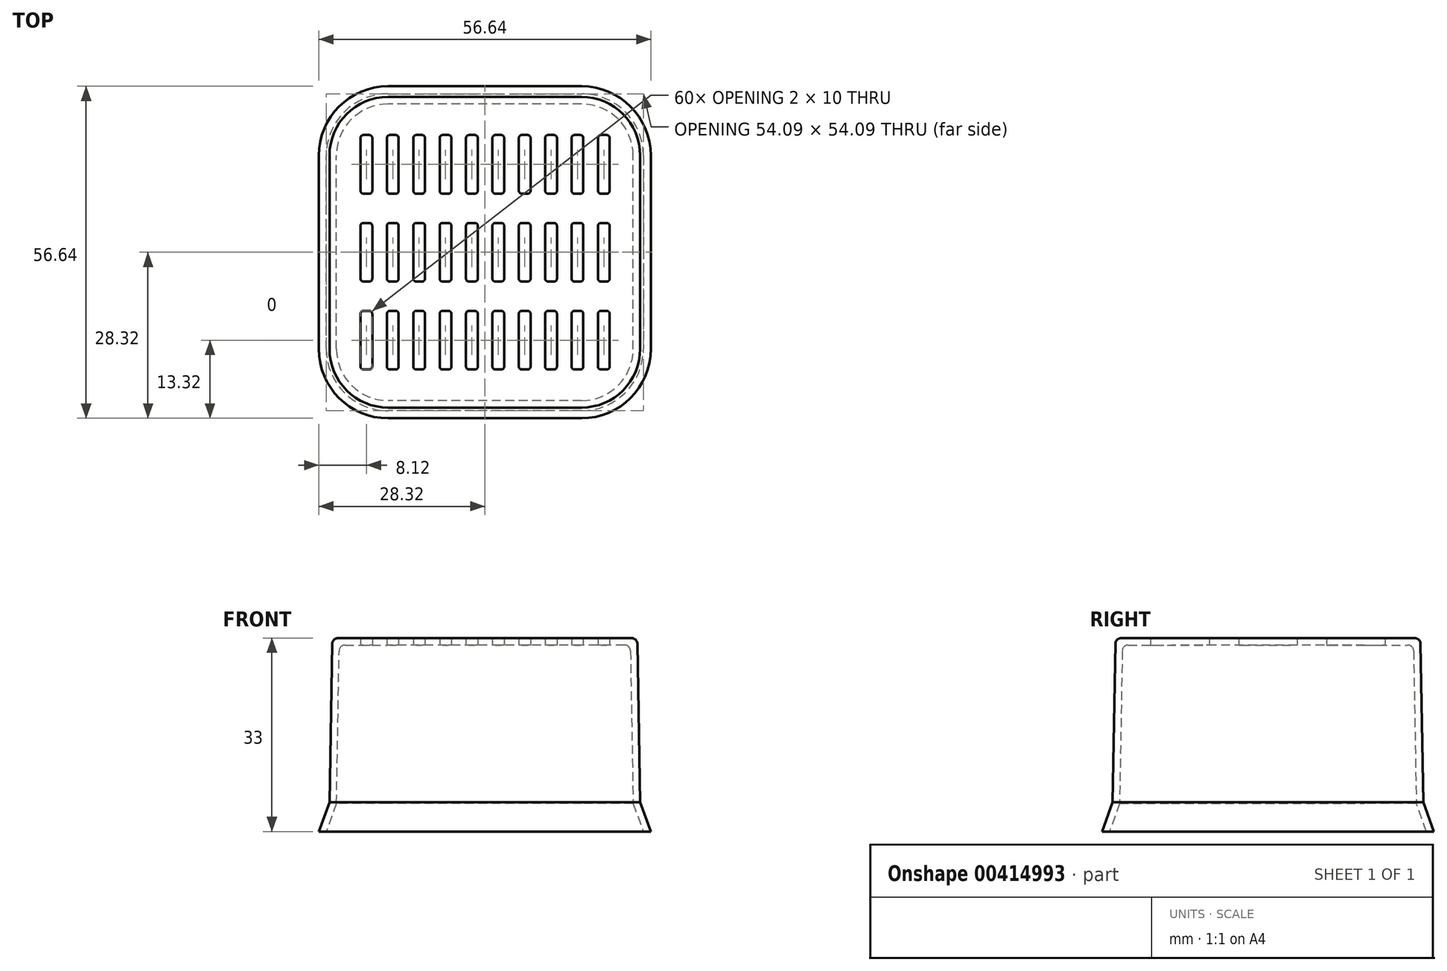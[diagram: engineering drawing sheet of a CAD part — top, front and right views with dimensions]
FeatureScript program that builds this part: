
annotation { "Feature Type Name" : "Feature", "Feature Type Description" : "" }
export const myFeature = defineFeature(function(context is Context, id is Id, definition is map)
    precondition{}
    {
        {
            var Q0;
            Q0=qCreatedBy(makeId("Top.planeOp"),FACE);
            var sketch = newSketch(context, id + "F0", { "sketchPlane" : qUnion([Q0])});
            skLineSegment(sketch, "E0.bottom", {"start": v(16.5, -26.5) * mm, "end": v(-16.5, -26.5) * mm});
            skLineSegment(sketch, "E0.top", {"start": v(16.5, 26.5) * mm, "end": v(-16.5, 26.5) * mm});
            skLineSegment(sketch, "E0.left", {"start": v(26.5, -16.5) * mm, "end": v(26.5, 16.5) * mm});
            skLineSegment(sketch, "E0.right", {"start": v(-26.5, -16.5) * mm, "end": v(-26.5, 16.5) * mm});
            skPoint(sketch, "E0.middle", {"position": v(0, 0) * mm});
            skPoint(sketch, "E1.visualSharp", {"position": v(-26.5, 26.5) * mm});
            skArc(sketch, "E1.filletArc", {"start": v(-16.5, 26.5) * mm, "mid": v(-23.57, 23.57) * mm, "end": v(-26.5, 16.5) * mm});
            skPoint(sketch, "E2.visualSharp", {"position": v(-26.5, -26.5) * mm});
            skArc(sketch, "E2.filletArc", {"start": v(-26.5, -16.5) * mm, "mid": v(-23.57, -23.57) * mm, "end": v(-16.5, -26.5) * mm});
            skPoint(sketch, "E3.visualSharp", {"position": v(26.5, -26.5) * mm});
            skArc(sketch, "E3.filletArc", {"start": v(16.5, -26.5) * mm, "mid": v(23.57, -23.57) * mm, "end": v(26.5, -16.5) * mm});
            skPoint(sketch, "E4.visualSharp", {"position": v(26.5, 26.5) * mm});
            skArc(sketch, "E4.filletArc", {"start": v(26.5, 16.5) * mm, "mid": v(23.57, 23.57) * mm, "end": v(16.5, 26.5) * mm});
            skSolve(sketch);
        }
        {
            var Q0;
            Q0 = qSketchRegion(id + "F0", true);
            extrude(context, id + "F1", {"entities" : qUnion([Q0]), "depth" : 28 * mm, "hasDraft" : true, "draftAngle" : 1 * degree, "draftPullDirection" : true, "hasSecondDirection" : true, "secondDirectionOppositeDirection" : true, "secondDirectionDepth" : 5 * mm, "hasSecondDirectionDraft" : true, "secondDirectionDraftAngle" : 20 * degree});
        }
        {
            var Q0;
            Q0=makeQuery(id+"F1.opExtrude","CAP_FACE",FACE,{"disambiguationData":[OSD([sQuery(id+"F0.wireOp",EDGE,"E0.bottom"),sQuery(id+"F0.wireOp",EDGE,"E0.top"),sQuery(id+"F0.wireOp",EDGE,"E0.left"),sQuery(id+"F0.wireOp",EDGE,"E0.right"),sQuery(id+"F0.wireOp",EDGE,"E1.filletArc"),sQuery(id+"F0.wireOp",EDGE,"E2.filletArc"),sQuery(id+"F0.wireOp",EDGE,"E3.filletArc"),sQuery(id+"F0.wireOp",EDGE,"E4.filletArc")])],"isStart":true});
            shell(context, id + "F2", {"entities" : qUnion([Q0]), "thickness" : 1.2 * mm});
        }
        {
            var Q0;
            Q0=makeQuery(id+"F2.opShell","OFFSET_FACE",FACE,{"disambiguationData":[OSD([sQuery(id+"F0.wireOp",EDGE,"E0.bottom"),sQuery(id+"F0.wireOp",EDGE,"E0.top"),sQuery(id+"F0.wireOp",EDGE,"E0.left"),sQuery(id+"F0.wireOp",EDGE,"E0.right"),sQuery(id+"F0.wireOp",EDGE,"E1.filletArc"),sQuery(id+"F0.wireOp",EDGE,"E2.filletArc"),sQuery(id+"F0.wireOp",EDGE,"E3.filletArc"),sQuery(id+"F0.wireOp",EDGE,"E4.filletArc")])]});
            var sketch = newSketch(context, id + "F3", { "sketchPlane" : qUnion([Q0])});
            skLineSegment(sketch, "E5.bottom", {"start": v(-20.7, -10) * mm, "end": v(-19.7, -10) * mm});
            skLineSegment(sketch, "E5.top", {"start": v(-20.7, -20) * mm, "end": v(-19.7, -20) * mm});
            skLineSegment(sketch, "E5.left", {"start": v(-21.2, -10.5) * mm, "end": v(-21.2, -19.5) * mm});
            skLineSegment(sketch, "E5.right", {"start": v(-19.2, -10.5) * mm, "end": v(-19.2, -19.5) * mm});
            skPoint(sketch, "E6.visualSharp", {"position": v(-21.2, -10) * mm});
            skArc(sketch, "E6.filletArc", {"start": v(-20.7, -10) * mm, "mid": v(-21.05, -10.15) * mm, "end": v(-21.2, -10.5) * mm});
            skPoint(sketch, "E7.visualSharp", {"position": v(-19.2, -10) * mm});
            skArc(sketch, "E7.filletArc", {"start": v(-19.2, -10.5) * mm, "mid": v(-19.35, -10.15) * mm, "end": v(-19.7, -10) * mm});
            skPoint(sketch, "E8.visualSharp", {"position": v(-21.2, -20) * mm});
            skArc(sketch, "E8.filletArc", {"start": v(-21.2, -19.5) * mm, "mid": v(-21.05, -19.85) * mm, "end": v(-20.7, -20) * mm});
            skPoint(sketch, "E9.visualSharp", {"position": v(-19.2, -20) * mm});
            skArc(sketch, "E9.filletArc", {"start": v(-19.7, -20) * mm, "mid": v(-19.35, -19.85) * mm, "end": v(-19.2, -19.5) * mm});
            skLineSegment(sketch, "E10.0.1.0", {"start": v(-21.2, 4.5) * mm, "end": v(-21.2, -4.5) * mm});
            skArc(sketch, "E10.0.1.1", {"start": v(-20.7, 5) * mm, "mid": v(-21.05, 4.85) * mm, "end": v(-21.2, 4.5) * mm});
            skArc(sketch, "E10.0.1.2", {"start": v(-19.7, -5) * mm, "mid": v(-19.35, -4.85) * mm, "end": v(-19.2, -4.5) * mm});
            skArc(sketch, "E10.0.1.3", {"start": v(-19.2, 4.5) * mm, "mid": v(-19.35, 4.85) * mm, "end": v(-19.7, 5) * mm});
            skArc(sketch, "E10.0.1.4", {"start": v(-21.2, -4.5) * mm, "mid": v(-21.05, -4.85) * mm, "end": v(-20.7, -5) * mm});
            skLineSegment(sketch, "E10.0.1.5", {"start": v(-19.2, 4.5) * mm, "end": v(-19.2, -4.5) * mm});
            skLineSegment(sketch, "E10.0.1.6", {"start": v(-20.7, 5) * mm, "end": v(-19.7, 5) * mm});
            skLineSegment(sketch, "E10.0.1.7", {"start": v(-20.7, -5) * mm, "end": v(-19.7, -5) * mm});
            skLineSegment(sketch, "E10.0.2.0", {"start": v(-21.2, 19.5) * mm, "end": v(-21.2, 10.5) * mm});
            skArc(sketch, "E10.0.2.1", {"start": v(-20.7, 20) * mm, "mid": v(-21.05, 19.85) * mm, "end": v(-21.2, 19.5) * mm});
            skArc(sketch, "E10.0.2.2", {"start": v(-19.7, 10) * mm, "mid": v(-19.35, 10.15) * mm, "end": v(-19.2, 10.5) * mm});
            skArc(sketch, "E10.0.2.3", {"start": v(-19.2, 19.5) * mm, "mid": v(-19.35, 19.85) * mm, "end": v(-19.7, 20) * mm});
            skArc(sketch, "E10.0.2.4", {"start": v(-21.2, 10.5) * mm, "mid": v(-21.05, 10.15) * mm, "end": v(-20.7, 10) * mm});
            skLineSegment(sketch, "E10.0.2.5", {"start": v(-19.2, 19.5) * mm, "end": v(-19.2, 10.5) * mm});
            skLineSegment(sketch, "E10.0.2.6", {"start": v(-20.7, 20) * mm, "end": v(-19.7, 20) * mm});
            skLineSegment(sketch, "E10.0.2.7", {"start": v(-20.7, 10) * mm, "end": v(-19.7, 10) * mm});
            skLineSegment(sketch, "E10.1.0.0", {"start": v(-16.7, -10.5) * mm, "end": v(-16.7, -19.5) * mm});
            skArc(sketch, "E10.1.0.1", {"start": v(-16.2, -10) * mm, "mid": v(-16.55, -10.15) * mm, "end": v(-16.7, -10.5) * mm});
            skArc(sketch, "E10.1.0.2", {"start": v(-15.2, -20) * mm, "mid": v(-14.85, -19.85) * mm, "end": v(-14.7, -19.5) * mm});
            skArc(sketch, "E10.1.0.3", {"start": v(-14.7, -10.5) * mm, "mid": v(-14.85, -10.15) * mm, "end": v(-15.2, -10) * mm});
            skArc(sketch, "E10.1.0.4", {"start": v(-16.7, -19.5) * mm, "mid": v(-16.55, -19.85) * mm, "end": v(-16.2, -20) * mm});
            skLineSegment(sketch, "E10.1.0.5", {"start": v(-14.7, -10.5) * mm, "end": v(-14.7, -19.5) * mm});
            skLineSegment(sketch, "E10.1.0.6", {"start": v(-16.2, -10) * mm, "end": v(-15.2, -10) * mm});
            skLineSegment(sketch, "E10.1.0.7", {"start": v(-16.2, -20) * mm, "end": v(-15.2, -20) * mm});
            skLineSegment(sketch, "E10.1.1.0", {"start": v(-16.7, 4.5) * mm, "end": v(-16.7, -4.5) * mm});
            skArc(sketch, "E10.1.1.1", {"start": v(-16.2, 5) * mm, "mid": v(-16.55, 4.85) * mm, "end": v(-16.7, 4.5) * mm});
            skArc(sketch, "E10.1.1.2", {"start": v(-15.2, -5) * mm, "mid": v(-14.85, -4.85) * mm, "end": v(-14.7, -4.5) * mm});
            skArc(sketch, "E10.1.1.3", {"start": v(-14.7, 4.5) * mm, "mid": v(-14.85, 4.85) * mm, "end": v(-15.2, 5) * mm});
            skArc(sketch, "E10.1.1.4", {"start": v(-16.7, -4.5) * mm, "mid": v(-16.55, -4.85) * mm, "end": v(-16.2, -5) * mm});
            skLineSegment(sketch, "E10.1.1.5", {"start": v(-14.7, 4.5) * mm, "end": v(-14.7, -4.5) * mm});
            skLineSegment(sketch, "E10.1.1.6", {"start": v(-16.2, 5) * mm, "end": v(-15.2, 5) * mm});
            skLineSegment(sketch, "E10.1.1.7", {"start": v(-16.2, -5) * mm, "end": v(-15.2, -5) * mm});
            skLineSegment(sketch, "E10.1.2.0", {"start": v(-16.7, 19.5) * mm, "end": v(-16.7, 10.5) * mm});
            skArc(sketch, "E10.1.2.1", {"start": v(-16.2, 20) * mm, "mid": v(-16.55, 19.85) * mm, "end": v(-16.7, 19.5) * mm});
            skArc(sketch, "E10.1.2.2", {"start": v(-15.2, 10) * mm, "mid": v(-14.85, 10.15) * mm, "end": v(-14.7, 10.5) * mm});
            skArc(sketch, "E10.1.2.3", {"start": v(-14.7, 19.5) * mm, "mid": v(-14.85, 19.85) * mm, "end": v(-15.2, 20) * mm});
            skArc(sketch, "E10.1.2.4", {"start": v(-16.7, 10.5) * mm, "mid": v(-16.55, 10.15) * mm, "end": v(-16.2, 10) * mm});
            skLineSegment(sketch, "E10.1.2.5", {"start": v(-14.7, 19.5) * mm, "end": v(-14.7, 10.5) * mm});
            skLineSegment(sketch, "E10.1.2.6", {"start": v(-16.2, 20) * mm, "end": v(-15.2, 20) * mm});
            skLineSegment(sketch, "E10.1.2.7", {"start": v(-16.2, 10) * mm, "end": v(-15.2, 10) * mm});
            skLineSegment(sketch, "E10.2.0.0", {"start": v(-12.2, -10.5) * mm, "end": v(-12.2, -19.5) * mm});
            skArc(sketch, "E10.2.0.1", {"start": v(-11.7, -10) * mm, "mid": v(-12.05, -10.15) * mm, "end": v(-12.2, -10.5) * mm});
            skArc(sketch, "E10.2.0.2", {"start": v(-10.7, -20) * mm, "mid": v(-10.35, -19.85) * mm, "end": v(-10.2, -19.5) * mm});
            skArc(sketch, "E10.2.0.3", {"start": v(-10.2, -10.5) * mm, "mid": v(-10.35, -10.15) * mm, "end": v(-10.7, -10) * mm});
            skArc(sketch, "E10.2.0.4", {"start": v(-12.2, -19.5) * mm, "mid": v(-12.05, -19.85) * mm, "end": v(-11.7, -20) * mm});
            skLineSegment(sketch, "E10.2.0.5", {"start": v(-10.2, -10.5) * mm, "end": v(-10.2, -19.5) * mm});
            skLineSegment(sketch, "E10.2.0.6", {"start": v(-11.7, -10) * mm, "end": v(-10.7, -10) * mm});
            skLineSegment(sketch, "E10.2.0.7", {"start": v(-11.7, -20) * mm, "end": v(-10.7, -20) * mm});
            skLineSegment(sketch, "E10.2.1.0", {"start": v(-12.2, 4.5) * mm, "end": v(-12.2, -4.5) * mm});
            skArc(sketch, "E10.2.1.1", {"start": v(-11.7, 5) * mm, "mid": v(-12.05, 4.85) * mm, "end": v(-12.2, 4.5) * mm});
            skArc(sketch, "E10.2.1.2", {"start": v(-10.7, -5) * mm, "mid": v(-10.35, -4.85) * mm, "end": v(-10.2, -4.5) * mm});
            skArc(sketch, "E10.2.1.3", {"start": v(-10.2, 4.5) * mm, "mid": v(-10.35, 4.85) * mm, "end": v(-10.7, 5) * mm});
            skArc(sketch, "E10.2.1.4", {"start": v(-12.2, -4.5) * mm, "mid": v(-12.05, -4.85) * mm, "end": v(-11.7, -5) * mm});
            skLineSegment(sketch, "E10.2.1.5", {"start": v(-10.2, 4.5) * mm, "end": v(-10.2, -4.5) * mm});
            skLineSegment(sketch, "E10.2.1.6", {"start": v(-11.7, 5) * mm, "end": v(-10.7, 5) * mm});
            skLineSegment(sketch, "E10.2.1.7", {"start": v(-11.7, -5) * mm, "end": v(-10.7, -5) * mm});
            skLineSegment(sketch, "E10.2.2.0", {"start": v(-12.2, 19.5) * mm, "end": v(-12.2, 10.5) * mm});
            skArc(sketch, "E10.2.2.1", {"start": v(-11.7, 20) * mm, "mid": v(-12.05, 19.85) * mm, "end": v(-12.2, 19.5) * mm});
            skArc(sketch, "E10.2.2.2", {"start": v(-10.7, 10) * mm, "mid": v(-10.35, 10.15) * mm, "end": v(-10.2, 10.5) * mm});
            skArc(sketch, "E10.2.2.3", {"start": v(-10.2, 19.5) * mm, "mid": v(-10.35, 19.85) * mm, "end": v(-10.7, 20) * mm});
            skArc(sketch, "E10.2.2.4", {"start": v(-12.2, 10.5) * mm, "mid": v(-12.05, 10.15) * mm, "end": v(-11.7, 10) * mm});
            skLineSegment(sketch, "E10.2.2.5", {"start": v(-10.2, 19.5) * mm, "end": v(-10.2, 10.5) * mm});
            skLineSegment(sketch, "E10.2.2.6", {"start": v(-11.7, 20) * mm, "end": v(-10.7, 20) * mm});
            skLineSegment(sketch, "E10.2.2.7", {"start": v(-11.7, 10) * mm, "end": v(-10.7, 10) * mm});
            skLineSegment(sketch, "E10.3.0.0", {"start": v(-7.7, -10.5) * mm, "end": v(-7.7, -19.5) * mm});
            skArc(sketch, "E10.3.0.1", {"start": v(-7.2, -10) * mm, "mid": v(-7.55, -10.15) * mm, "end": v(-7.7, -10.5) * mm});
            skArc(sketch, "E10.3.0.2", {"start": v(-6.2, -20) * mm, "mid": v(-5.85, -19.85) * mm, "end": v(-5.7, -19.5) * mm});
            skArc(sketch, "E10.3.0.3", {"start": v(-5.7, -10.5) * mm, "mid": v(-5.85, -10.15) * mm, "end": v(-6.2, -10) * mm});
            skArc(sketch, "E10.3.0.4", {"start": v(-7.7, -19.5) * mm, "mid": v(-7.55, -19.85) * mm, "end": v(-7.2, -20) * mm});
            skLineSegment(sketch, "E10.3.0.5", {"start": v(-5.7, -10.5) * mm, "end": v(-5.7, -19.5) * mm});
            skLineSegment(sketch, "E10.3.0.6", {"start": v(-7.2, -10) * mm, "end": v(-6.2, -10) * mm});
            skLineSegment(sketch, "E10.3.0.7", {"start": v(-7.2, -20) * mm, "end": v(-6.2, -20) * mm});
            skLineSegment(sketch, "E10.3.1.0", {"start": v(-7.7, 4.5) * mm, "end": v(-7.7, -4.5) * mm});
            skArc(sketch, "E10.3.1.1", {"start": v(-7.2, 5) * mm, "mid": v(-7.55, 4.85) * mm, "end": v(-7.7, 4.5) * mm});
            skArc(sketch, "E10.3.1.2", {"start": v(-6.2, -5) * mm, "mid": v(-5.85, -4.85) * mm, "end": v(-5.7, -4.5) * mm});
            skArc(sketch, "E10.3.1.3", {"start": v(-5.7, 4.5) * mm, "mid": v(-5.85, 4.85) * mm, "end": v(-6.2, 5) * mm});
            skArc(sketch, "E10.3.1.4", {"start": v(-7.7, -4.5) * mm, "mid": v(-7.55, -4.85) * mm, "end": v(-7.2, -5) * mm});
            skLineSegment(sketch, "E10.3.1.5", {"start": v(-5.7, 4.5) * mm, "end": v(-5.7, -4.5) * mm});
            skLineSegment(sketch, "E10.3.1.6", {"start": v(-7.2, 5) * mm, "end": v(-6.2, 5) * mm});
            skLineSegment(sketch, "E10.3.1.7", {"start": v(-7.2, -5) * mm, "end": v(-6.2, -5) * mm});
            skLineSegment(sketch, "E10.3.2.0", {"start": v(-7.7, 19.5) * mm, "end": v(-7.7, 10.5) * mm});
            skArc(sketch, "E10.3.2.1", {"start": v(-7.2, 20) * mm, "mid": v(-7.55, 19.85) * mm, "end": v(-7.7, 19.5) * mm});
            skArc(sketch, "E10.3.2.2", {"start": v(-6.2, 10) * mm, "mid": v(-5.85, 10.15) * mm, "end": v(-5.7, 10.5) * mm});
            skArc(sketch, "E10.3.2.3", {"start": v(-5.7, 19.5) * mm, "mid": v(-5.85, 19.85) * mm, "end": v(-6.2, 20) * mm});
            skArc(sketch, "E10.3.2.4", {"start": v(-7.7, 10.5) * mm, "mid": v(-7.55, 10.15) * mm, "end": v(-7.2, 10) * mm});
            skLineSegment(sketch, "E10.3.2.5", {"start": v(-5.7, 19.5) * mm, "end": v(-5.7, 10.5) * mm});
            skLineSegment(sketch, "E10.3.2.6", {"start": v(-7.2, 20) * mm, "end": v(-6.2, 20) * mm});
            skLineSegment(sketch, "E10.3.2.7", {"start": v(-7.2, 10) * mm, "end": v(-6.2, 10) * mm});
            skLineSegment(sketch, "E10.4.0.0", {"start": v(-3.2, -10.5) * mm, "end": v(-3.2, -19.5) * mm});
            skArc(sketch, "E10.4.0.1", {"start": v(-2.7, -10) * mm, "mid": v(-3.05, -10.15) * mm, "end": v(-3.2, -10.5) * mm});
            skArc(sketch, "E10.4.0.2", {"start": v(-1.7, -20) * mm, "mid": v(-1.35, -19.85) * mm, "end": v(-1.2, -19.5) * mm});
            skArc(sketch, "E10.4.0.3", {"start": v(-1.2, -10.5) * mm, "mid": v(-1.35, -10.15) * mm, "end": v(-1.7, -10) * mm});
            skArc(sketch, "E10.4.0.4", {"start": v(-3.2, -19.5) * mm, "mid": v(-3.05, -19.85) * mm, "end": v(-2.7, -20) * mm});
            skLineSegment(sketch, "E10.4.0.5", {"start": v(-1.2, -10.5) * mm, "end": v(-1.2, -19.5) * mm});
            skLineSegment(sketch, "E10.4.0.6", {"start": v(-2.7, -10) * mm, "end": v(-1.7, -10) * mm});
            skLineSegment(sketch, "E10.4.0.7", {"start": v(-2.7, -20) * mm, "end": v(-1.7, -20) * mm});
            skLineSegment(sketch, "E10.4.1.0", {"start": v(-3.2, 4.5) * mm, "end": v(-3.2, -4.5) * mm});
            skArc(sketch, "E10.4.1.1", {"start": v(-2.7, 5) * mm, "mid": v(-3.05, 4.85) * mm, "end": v(-3.2, 4.5) * mm});
            skArc(sketch, "E10.4.1.2", {"start": v(-1.7, -5) * mm, "mid": v(-1.35, -4.85) * mm, "end": v(-1.2, -4.5) * mm});
            skArc(sketch, "E10.4.1.3", {"start": v(-1.2, 4.5) * mm, "mid": v(-1.35, 4.85) * mm, "end": v(-1.7, 5) * mm});
            skArc(sketch, "E10.4.1.4", {"start": v(-3.2, -4.5) * mm, "mid": v(-3.05, -4.85) * mm, "end": v(-2.7, -5) * mm});
            skLineSegment(sketch, "E10.4.1.5", {"start": v(-1.2, 4.5) * mm, "end": v(-1.2, -4.5) * mm});
            skLineSegment(sketch, "E10.4.1.6", {"start": v(-2.7, 5) * mm, "end": v(-1.7, 5) * mm});
            skLineSegment(sketch, "E10.4.1.7", {"start": v(-2.7, -5) * mm, "end": v(-1.7, -5) * mm});
            skLineSegment(sketch, "E10.4.2.0", {"start": v(-3.2, 19.5) * mm, "end": v(-3.2, 10.5) * mm});
            skArc(sketch, "E10.4.2.1", {"start": v(-2.7, 20) * mm, "mid": v(-3.05, 19.85) * mm, "end": v(-3.2, 19.5) * mm});
            skArc(sketch, "E10.4.2.2", {"start": v(-1.7, 10) * mm, "mid": v(-1.35, 10.15) * mm, "end": v(-1.2, 10.5) * mm});
            skArc(sketch, "E10.4.2.3", {"start": v(-1.2, 19.5) * mm, "mid": v(-1.35, 19.85) * mm, "end": v(-1.7, 20) * mm});
            skArc(sketch, "E10.4.2.4", {"start": v(-3.2, 10.5) * mm, "mid": v(-3.05, 10.15) * mm, "end": v(-2.7, 10) * mm});
            skLineSegment(sketch, "E10.4.2.5", {"start": v(-1.2, 19.5) * mm, "end": v(-1.2, 10.5) * mm});
            skLineSegment(sketch, "E10.4.2.6", {"start": v(-2.7, 20) * mm, "end": v(-1.7, 20) * mm});
            skLineSegment(sketch, "E10.4.2.7", {"start": v(-2.7, 10) * mm, "end": v(-1.7, 10) * mm});
            skLineSegment(sketch, "E10.5.0.0", {"start": v(1.3, -10.5) * mm, "end": v(1.3, -19.5) * mm});
            skArc(sketch, "E10.5.0.1", {"start": v(1.8, -10) * mm, "mid": v(1.45, -10.15) * mm, "end": v(1.3, -10.5) * mm});
            skArc(sketch, "E10.5.0.2", {"start": v(2.8, -20) * mm, "mid": v(3.15, -19.85) * mm, "end": v(3.3, -19.5) * mm});
            skArc(sketch, "E10.5.0.3", {"start": v(3.3, -10.5) * mm, "mid": v(3.15, -10.15) * mm, "end": v(2.8, -10) * mm});
            skArc(sketch, "E10.5.0.4", {"start": v(1.3, -19.5) * mm, "mid": v(1.45, -19.85) * mm, "end": v(1.8, -20) * mm});
            skLineSegment(sketch, "E10.5.0.5", {"start": v(3.3, -10.5) * mm, "end": v(3.3, -19.5) * mm});
            skLineSegment(sketch, "E10.5.0.6", {"start": v(1.8, -10) * mm, "end": v(2.8, -10) * mm});
            skLineSegment(sketch, "E10.5.0.7", {"start": v(1.8, -20) * mm, "end": v(2.8, -20) * mm});
            skLineSegment(sketch, "E10.5.1.0", {"start": v(1.3, 4.5) * mm, "end": v(1.3, -4.5) * mm});
            skArc(sketch, "E10.5.1.1", {"start": v(1.8, 5) * mm, "mid": v(1.45, 4.85) * mm, "end": v(1.3, 4.5) * mm});
            skArc(sketch, "E10.5.1.2", {"start": v(2.8, -5) * mm, "mid": v(3.15, -4.85) * mm, "end": v(3.3, -4.5) * mm});
            skArc(sketch, "E10.5.1.3", {"start": v(3.3, 4.5) * mm, "mid": v(3.15, 4.85) * mm, "end": v(2.8, 5) * mm});
            skArc(sketch, "E10.5.1.4", {"start": v(1.3, -4.5) * mm, "mid": v(1.45, -4.85) * mm, "end": v(1.8, -5) * mm});
            skLineSegment(sketch, "E10.5.1.5", {"start": v(3.3, 4.5) * mm, "end": v(3.3, -4.5) * mm});
            skLineSegment(sketch, "E10.5.1.6", {"start": v(1.8, 5) * mm, "end": v(2.8, 5) * mm});
            skLineSegment(sketch, "E10.5.1.7", {"start": v(1.8, -5) * mm, "end": v(2.8, -5) * mm});
            skLineSegment(sketch, "E10.5.2.0", {"start": v(1.3, 19.5) * mm, "end": v(1.3, 10.5) * mm});
            skArc(sketch, "E10.5.2.1", {"start": v(1.8, 20) * mm, "mid": v(1.45, 19.85) * mm, "end": v(1.3, 19.5) * mm});
            skArc(sketch, "E10.5.2.2", {"start": v(2.8, 10) * mm, "mid": v(3.15, 10.15) * mm, "end": v(3.3, 10.5) * mm});
            skArc(sketch, "E10.5.2.3", {"start": v(3.3, 19.5) * mm, "mid": v(3.15, 19.85) * mm, "end": v(2.8, 20) * mm});
            skArc(sketch, "E10.5.2.4", {"start": v(1.3, 10.5) * mm, "mid": v(1.45, 10.15) * mm, "end": v(1.8, 10) * mm});
            skLineSegment(sketch, "E10.5.2.5", {"start": v(3.3, 19.5) * mm, "end": v(3.3, 10.5) * mm});
            skLineSegment(sketch, "E10.5.2.6", {"start": v(1.8, 20) * mm, "end": v(2.8, 20) * mm});
            skLineSegment(sketch, "E10.5.2.7", {"start": v(1.8, 10) * mm, "end": v(2.8, 10) * mm});
            skLineSegment(sketch, "E10.6.0.0", {"start": v(5.8, -10.5) * mm, "end": v(5.8, -19.5) * mm});
            skArc(sketch, "E10.6.0.1", {"start": v(6.3, -10) * mm, "mid": v(5.95, -10.15) * mm, "end": v(5.8, -10.5) * mm});
            skArc(sketch, "E10.6.0.2", {"start": v(7.3, -20) * mm, "mid": v(7.65, -19.85) * mm, "end": v(7.8, -19.5) * mm});
            skArc(sketch, "E10.6.0.3", {"start": v(7.8, -10.5) * mm, "mid": v(7.65, -10.15) * mm, "end": v(7.3, -10) * mm});
            skArc(sketch, "E10.6.0.4", {"start": v(5.8, -19.5) * mm, "mid": v(5.95, -19.85) * mm, "end": v(6.3, -20) * mm});
            skLineSegment(sketch, "E10.6.0.5", {"start": v(7.8, -10.5) * mm, "end": v(7.8, -19.5) * mm});
            skLineSegment(sketch, "E10.6.0.6", {"start": v(6.3, -10) * mm, "end": v(7.3, -10) * mm});
            skLineSegment(sketch, "E10.6.0.7", {"start": v(6.3, -20) * mm, "end": v(7.3, -20) * mm});
            skLineSegment(sketch, "E10.6.1.0", {"start": v(5.8, 4.5) * mm, "end": v(5.8, -4.5) * mm});
            skArc(sketch, "E10.6.1.1", {"start": v(6.3, 5) * mm, "mid": v(5.95, 4.85) * mm, "end": v(5.8, 4.5) * mm});
            skArc(sketch, "E10.6.1.2", {"start": v(7.3, -5) * mm, "mid": v(7.65, -4.85) * mm, "end": v(7.8, -4.5) * mm});
            skArc(sketch, "E10.6.1.3", {"start": v(7.8, 4.5) * mm, "mid": v(7.65, 4.85) * mm, "end": v(7.3, 5) * mm});
            skArc(sketch, "E10.6.1.4", {"start": v(5.8, -4.5) * mm, "mid": v(5.95, -4.85) * mm, "end": v(6.3, -5) * mm});
            skLineSegment(sketch, "E10.6.1.5", {"start": v(7.8, 4.5) * mm, "end": v(7.8, -4.5) * mm});
            skLineSegment(sketch, "E10.6.1.6", {"start": v(6.3, 5) * mm, "end": v(7.3, 5) * mm});
            skLineSegment(sketch, "E10.6.1.7", {"start": v(6.3, -5) * mm, "end": v(7.3, -5) * mm});
            skLineSegment(sketch, "E10.6.2.0", {"start": v(5.8, 19.5) * mm, "end": v(5.8, 10.5) * mm});
            skArc(sketch, "E10.6.2.1", {"start": v(6.3, 20) * mm, "mid": v(5.95, 19.85) * mm, "end": v(5.8, 19.5) * mm});
            skArc(sketch, "E10.6.2.2", {"start": v(7.3, 10) * mm, "mid": v(7.65, 10.15) * mm, "end": v(7.8, 10.5) * mm});
            skArc(sketch, "E10.6.2.3", {"start": v(7.8, 19.5) * mm, "mid": v(7.65, 19.85) * mm, "end": v(7.3, 20) * mm});
            skArc(sketch, "E10.6.2.4", {"start": v(5.8, 10.5) * mm, "mid": v(5.95, 10.15) * mm, "end": v(6.3, 10) * mm});
            skLineSegment(sketch, "E10.6.2.5", {"start": v(7.8, 19.5) * mm, "end": v(7.8, 10.5) * mm});
            skLineSegment(sketch, "E10.6.2.6", {"start": v(6.3, 20) * mm, "end": v(7.3, 20) * mm});
            skLineSegment(sketch, "E10.6.2.7", {"start": v(6.3, 10) * mm, "end": v(7.3, 10) * mm});
            skLineSegment(sketch, "E10.7.0.0", {"start": v(10.3, -10.5) * mm, "end": v(10.3, -19.5) * mm});
            skArc(sketch, "E10.7.0.1", {"start": v(10.8, -10) * mm, "mid": v(10.45, -10.15) * mm, "end": v(10.3, -10.5) * mm});
            skArc(sketch, "E10.7.0.2", {"start": v(11.8, -20) * mm, "mid": v(12.15, -19.85) * mm, "end": v(12.3, -19.5) * mm});
            skArc(sketch, "E10.7.0.3", {"start": v(12.3, -10.5) * mm, "mid": v(12.15, -10.15) * mm, "end": v(11.8, -10) * mm});
            skArc(sketch, "E10.7.0.4", {"start": v(10.3, -19.5) * mm, "mid": v(10.45, -19.85) * mm, "end": v(10.8, -20) * mm});
            skLineSegment(sketch, "E10.7.0.5", {"start": v(12.3, -10.5) * mm, "end": v(12.3, -19.5) * mm});
            skLineSegment(sketch, "E10.7.0.6", {"start": v(10.8, -10) * mm, "end": v(11.8, -10) * mm});
            skLineSegment(sketch, "E10.7.0.7", {"start": v(10.8, -20) * mm, "end": v(11.8, -20) * mm});
            skLineSegment(sketch, "E10.7.1.0", {"start": v(10.3, 4.5) * mm, "end": v(10.3, -4.5) * mm});
            skArc(sketch, "E10.7.1.1", {"start": v(10.8, 5) * mm, "mid": v(10.45, 4.85) * mm, "end": v(10.3, 4.5) * mm});
            skArc(sketch, "E10.7.1.2", {"start": v(11.8, -5) * mm, "mid": v(12.15, -4.85) * mm, "end": v(12.3, -4.5) * mm});
            skArc(sketch, "E10.7.1.3", {"start": v(12.3, 4.5) * mm, "mid": v(12.15, 4.85) * mm, "end": v(11.8, 5) * mm});
            skArc(sketch, "E10.7.1.4", {"start": v(10.3, -4.5) * mm, "mid": v(10.45, -4.85) * mm, "end": v(10.8, -5) * mm});
            skLineSegment(sketch, "E10.7.1.5", {"start": v(12.3, 4.5) * mm, "end": v(12.3, -4.5) * mm});
            skLineSegment(sketch, "E10.7.1.6", {"start": v(10.8, 5) * mm, "end": v(11.8, 5) * mm});
            skLineSegment(sketch, "E10.7.1.7", {"start": v(10.8, -5) * mm, "end": v(11.8, -5) * mm});
            skLineSegment(sketch, "E10.7.2.0", {"start": v(10.3, 19.5) * mm, "end": v(10.3, 10.5) * mm});
            skArc(sketch, "E10.7.2.1", {"start": v(10.8, 20) * mm, "mid": v(10.45, 19.85) * mm, "end": v(10.3, 19.5) * mm});
            skArc(sketch, "E10.7.2.2", {"start": v(11.8, 10) * mm, "mid": v(12.15, 10.15) * mm, "end": v(12.3, 10.5) * mm});
            skArc(sketch, "E10.7.2.3", {"start": v(12.3, 19.5) * mm, "mid": v(12.15, 19.85) * mm, "end": v(11.8, 20) * mm});
            skArc(sketch, "E10.7.2.4", {"start": v(10.3, 10.5) * mm, "mid": v(10.45, 10.15) * mm, "end": v(10.8, 10) * mm});
            skLineSegment(sketch, "E10.7.2.5", {"start": v(12.3, 19.5) * mm, "end": v(12.3, 10.5) * mm});
            skLineSegment(sketch, "E10.7.2.6", {"start": v(10.8, 20) * mm, "end": v(11.8, 20) * mm});
            skLineSegment(sketch, "E10.7.2.7", {"start": v(10.8, 10) * mm, "end": v(11.8, 10) * mm});
            skLineSegment(sketch, "E10.8.0.0", {"start": v(14.8, -10.5) * mm, "end": v(14.8, -19.5) * mm});
            skArc(sketch, "E10.8.0.1", {"start": v(15.3, -10) * mm, "mid": v(14.95, -10.15) * mm, "end": v(14.8, -10.5) * mm});
            skArc(sketch, "E10.8.0.2", {"start": v(16.3, -20) * mm, "mid": v(16.65, -19.85) * mm, "end": v(16.8, -19.5) * mm});
            skArc(sketch, "E10.8.0.3", {"start": v(16.8, -10.5) * mm, "mid": v(16.65, -10.15) * mm, "end": v(16.3, -10) * mm});
            skArc(sketch, "E10.8.0.4", {"start": v(14.8, -19.5) * mm, "mid": v(14.95, -19.85) * mm, "end": v(15.3, -20) * mm});
            skLineSegment(sketch, "E10.8.0.5", {"start": v(16.8, -10.5) * mm, "end": v(16.8, -19.5) * mm});
            skLineSegment(sketch, "E10.8.0.6", {"start": v(15.3, -10) * mm, "end": v(16.3, -10) * mm});
            skLineSegment(sketch, "E10.8.0.7", {"start": v(15.3, -20) * mm, "end": v(16.3, -20) * mm});
            skLineSegment(sketch, "E10.8.1.0", {"start": v(14.8, 4.5) * mm, "end": v(14.8, -4.5) * mm});
            skArc(sketch, "E10.8.1.1", {"start": v(15.3, 5) * mm, "mid": v(14.95, 4.85) * mm, "end": v(14.8, 4.5) * mm});
            skArc(sketch, "E10.8.1.2", {"start": v(16.3, -5) * mm, "mid": v(16.65, -4.85) * mm, "end": v(16.8, -4.5) * mm});
            skArc(sketch, "E10.8.1.3", {"start": v(16.8, 4.5) * mm, "mid": v(16.65, 4.85) * mm, "end": v(16.3, 5) * mm});
            skArc(sketch, "E10.8.1.4", {"start": v(14.8, -4.5) * mm, "mid": v(14.95, -4.85) * mm, "end": v(15.3, -5) * mm});
            skLineSegment(sketch, "E10.8.1.5", {"start": v(16.8, 4.5) * mm, "end": v(16.8, -4.5) * mm});
            skLineSegment(sketch, "E10.8.1.6", {"start": v(15.3, 5) * mm, "end": v(16.3, 5) * mm});
            skLineSegment(sketch, "E10.8.1.7", {"start": v(15.3, -5) * mm, "end": v(16.3, -5) * mm});
            skLineSegment(sketch, "E10.8.2.0", {"start": v(14.8, 19.5) * mm, "end": v(14.8, 10.5) * mm});
            skArc(sketch, "E10.8.2.1", {"start": v(15.3, 20) * mm, "mid": v(14.95, 19.85) * mm, "end": v(14.8, 19.5) * mm});
            skArc(sketch, "E10.8.2.2", {"start": v(16.3, 10) * mm, "mid": v(16.65, 10.15) * mm, "end": v(16.8, 10.5) * mm});
            skArc(sketch, "E10.8.2.3", {"start": v(16.8, 19.5) * mm, "mid": v(16.65, 19.85) * mm, "end": v(16.3, 20) * mm});
            skArc(sketch, "E10.8.2.4", {"start": v(14.8, 10.5) * mm, "mid": v(14.95, 10.15) * mm, "end": v(15.3, 10) * mm});
            skLineSegment(sketch, "E10.8.2.5", {"start": v(16.8, 19.5) * mm, "end": v(16.8, 10.5) * mm});
            skLineSegment(sketch, "E10.8.2.6", {"start": v(15.3, 20) * mm, "end": v(16.3, 20) * mm});
            skLineSegment(sketch, "E10.8.2.7", {"start": v(15.3, 10) * mm, "end": v(16.3, 10) * mm});
            skLineSegment(sketch, "E10.9.0.0", {"start": v(19.3, -10.5) * mm, "end": v(19.3, -19.5) * mm});
            skArc(sketch, "E10.9.0.1", {"start": v(19.8, -10) * mm, "mid": v(19.45, -10.15) * mm, "end": v(19.3, -10.5) * mm});
            skArc(sketch, "E10.9.0.2", {"start": v(20.8, -20) * mm, "mid": v(21.15, -19.85) * mm, "end": v(21.3, -19.5) * mm});
            skArc(sketch, "E10.9.0.3", {"start": v(21.3, -10.5) * mm, "mid": v(21.15, -10.15) * mm, "end": v(20.8, -10) * mm});
            skArc(sketch, "E10.9.0.4", {"start": v(19.3, -19.5) * mm, "mid": v(19.45, -19.85) * mm, "end": v(19.8, -20) * mm});
            skLineSegment(sketch, "E10.9.0.5", {"start": v(21.3, -10.5) * mm, "end": v(21.3, -19.5) * mm});
            skLineSegment(sketch, "E10.9.0.6", {"start": v(19.8, -10) * mm, "end": v(20.8, -10) * mm});
            skLineSegment(sketch, "E10.9.0.7", {"start": v(19.8, -20) * mm, "end": v(20.8, -20) * mm});
            skLineSegment(sketch, "E10.9.1.0", {"start": v(19.3, 4.5) * mm, "end": v(19.3, -4.5) * mm});
            skArc(sketch, "E10.9.1.1", {"start": v(19.8, 5) * mm, "mid": v(19.45, 4.85) * mm, "end": v(19.3, 4.5) * mm});
            skArc(sketch, "E10.9.1.2", {"start": v(20.8, -5) * mm, "mid": v(21.15, -4.85) * mm, "end": v(21.3, -4.5) * mm});
            skArc(sketch, "E10.9.1.3", {"start": v(21.3, 4.5) * mm, "mid": v(21.15, 4.85) * mm, "end": v(20.8, 5) * mm});
            skArc(sketch, "E10.9.1.4", {"start": v(19.3, -4.5) * mm, "mid": v(19.45, -4.85) * mm, "end": v(19.8, -5) * mm});
            skLineSegment(sketch, "E10.9.1.5", {"start": v(21.3, 4.5) * mm, "end": v(21.3, -4.5) * mm});
            skLineSegment(sketch, "E10.9.1.6", {"start": v(19.8, 5) * mm, "end": v(20.8, 5) * mm});
            skLineSegment(sketch, "E10.9.1.7", {"start": v(19.8, -5) * mm, "end": v(20.8, -5) * mm});
            skLineSegment(sketch, "E10.9.2.0", {"start": v(19.3, 19.5) * mm, "end": v(19.3, 10.5) * mm});
            skArc(sketch, "E10.9.2.1", {"start": v(19.8, 20) * mm, "mid": v(19.45, 19.85) * mm, "end": v(19.3, 19.5) * mm});
            skArc(sketch, "E10.9.2.2", {"start": v(20.8, 10) * mm, "mid": v(21.15, 10.15) * mm, "end": v(21.3, 10.5) * mm});
            skArc(sketch, "E10.9.2.3", {"start": v(21.3, 19.5) * mm, "mid": v(21.15, 19.85) * mm, "end": v(20.8, 20) * mm});
            skArc(sketch, "E10.9.2.4", {"start": v(19.3, 10.5) * mm, "mid": v(19.45, 10.15) * mm, "end": v(19.8, 10) * mm});
            skLineSegment(sketch, "E10.9.2.5", {"start": v(21.3, 19.5) * mm, "end": v(21.3, 10.5) * mm});
            skLineSegment(sketch, "E10.9.2.6", {"start": v(19.8, 20) * mm, "end": v(20.8, 20) * mm});
            skLineSegment(sketch, "E10.9.2.7", {"start": v(19.8, 10) * mm, "end": v(20.8, 10) * mm});
            skLineSegment(sketch, "E10.direction1", {"start": v(-21.2, -10.5) * mm, "end": v(-16.7, -10.5) * mm, "construction": true});
            skLineSegment(sketch, "E10.direction2", {"start": v(-21.2, -10.5) * mm, "end": v(-21.2, 4.5) * mm, "construction": true});
            skSolve(sketch);
        }
        {
            var Q0;
            Q0 = qSketchRegion(id + "F3", true);
            extrude(context, id + "F4", {"entities" : qUnion([Q0]), "operationType" : NewBodyOperationType.REMOVE, "oppositeDirection" : true, "depth" : 25.4 * mm});
        }
        {
            var Q0;
            {var subQ0=sQuery(id+"F0.wireOp",EDGE,"E4.filletArc");Q0=makeQuery(id+"F2.opShell","OFFSET_EDGE",EDGE,{"disambiguationData":[OSD([subQ0]),TDD([makeQuery(id+"F1.opExtrude","CAP_EDGE",EDGE,{"disambiguationData":[OSD([subQ0])],"isStart":false})])]});}
            var Q1;
            Q1=makeQuery(id+"F1.opExtrude","CAP_EDGE",EDGE,{"disambiguationData":[OSD([sQuery(id+"F0.wireOp",EDGE,"E0.bottom")])],"isStart":false});
            fillet(context, id + "F5", {"entities" : qUnion([Q0, Q1]), "radius" : 1 * mm, "tangentPropagation" : true, "allowEdgeOverflow" : false});
        }
    });
